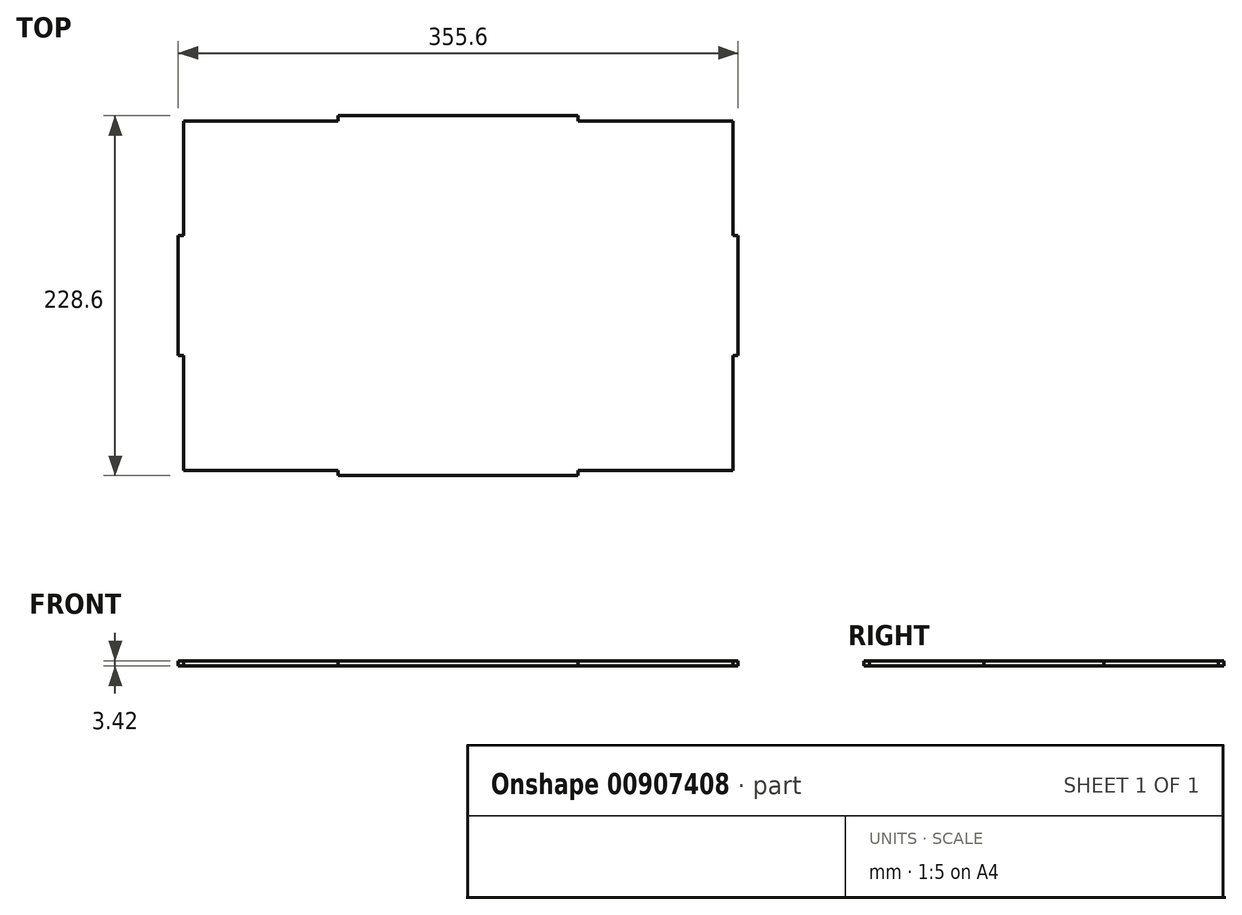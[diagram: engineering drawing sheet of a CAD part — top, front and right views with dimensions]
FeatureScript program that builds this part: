
annotation { "Feature Type Name" : "Feature", "Feature Type Description" : "" }
export const myFeature = defineFeature(function(context is Context, id is Id, definition is map)
    precondition{}
    {
        {
            var Q0;
            Q0=qCreatedBy(makeId("Top.planeOp"),FACE);
            var sketch = newSketch(context, id + "F0", { "sketchPlane" : qUnion([Q0])});
            skLineSegment(sketch, "E0", {"start": v(-76.2, -114.3) * mm, "end": v(76.2, -114.3) * mm});
            skLineSegment(sketch, "E1", {"start": v(76.2, -114.3) * mm, "end": v(76.2, -110.88) * mm});
            skLineSegment(sketch, "E2", {"start": v(76.2, -110.88) * mm, "end": v(174.38, -110.88) * mm});
            skLineSegment(sketch, "E3", {"start": v(174.38, -110.88) * mm, "end": v(174.38, -38.1) * mm});
            skLineSegment(sketch, "E4", {"start": v(174.38, -38.1) * mm, "end": v(177.8, -38.1) * mm});
            skLineSegment(sketch, "E5", {"start": v(177.8, -38.1) * mm, "end": v(177.8, 38.1) * mm});
            skLineSegment(sketch, "E6", {"start": v(177.8, 38.1) * mm, "end": v(174.38, 38.1) * mm});
            skLineSegment(sketch, "E7", {"start": v(174.38, 38.1) * mm, "end": v(174.38, 110.88) * mm});
            skLineSegment(sketch, "E8", {"start": v(174.38, 110.88) * mm, "end": v(76.2, 110.88) * mm});
            skLineSegment(sketch, "E9", {"start": v(76.2, 110.88) * mm, "end": v(76.2, 114.3) * mm});
            skLineSegment(sketch, "E10", {"start": v(76.2, 114.3) * mm, "end": v(-76.2, 114.3) * mm});
            skLineSegment(sketch, "E11", {"start": v(-76.2, 114.3) * mm, "end": v(-76.2, 110.88) * mm});
            skLineSegment(sketch, "E12", {"start": v(-76.2, 110.88) * mm, "end": v(-174.38, 110.88) * mm});
            skLineSegment(sketch, "E13", {"start": v(-174.38, 110.88) * mm, "end": v(-174.38, 38.1) * mm});
            skLineSegment(sketch, "E14", {"start": v(-174.38, 38.1) * mm, "end": v(-177.8, 38.1) * mm});
            skLineSegment(sketch, "E15", {"start": v(-177.8, 38.1) * mm, "end": v(-177.8, -38.1) * mm});
            skLineSegment(sketch, "E16", {"start": v(-177.8, -38.1) * mm, "end": v(-174.38, -38.1) * mm});
            skLineSegment(sketch, "E17", {"start": v(-174.38, -38.1) * mm, "end": v(-174.38, -110.88) * mm});
            skLineSegment(sketch, "E18", {"start": v(-174.38, -110.88) * mm, "end": v(-76.2, -110.88) * mm});
            skLineSegment(sketch, "E19", {"start": v(-76.2, -110.88) * mm, "end": v(-76.2, -114.3) * mm});
            skSolve(sketch);
        }
        {
            var Q0;
            Q0 = qSketchRegion(id + "F0", true);
            extrude(context, id + "F1", {"entities" : qUnion([Q0]), "depth" : 3.42 * mm, "offsetDistance" : 25.4 * mm});
        }
    });
